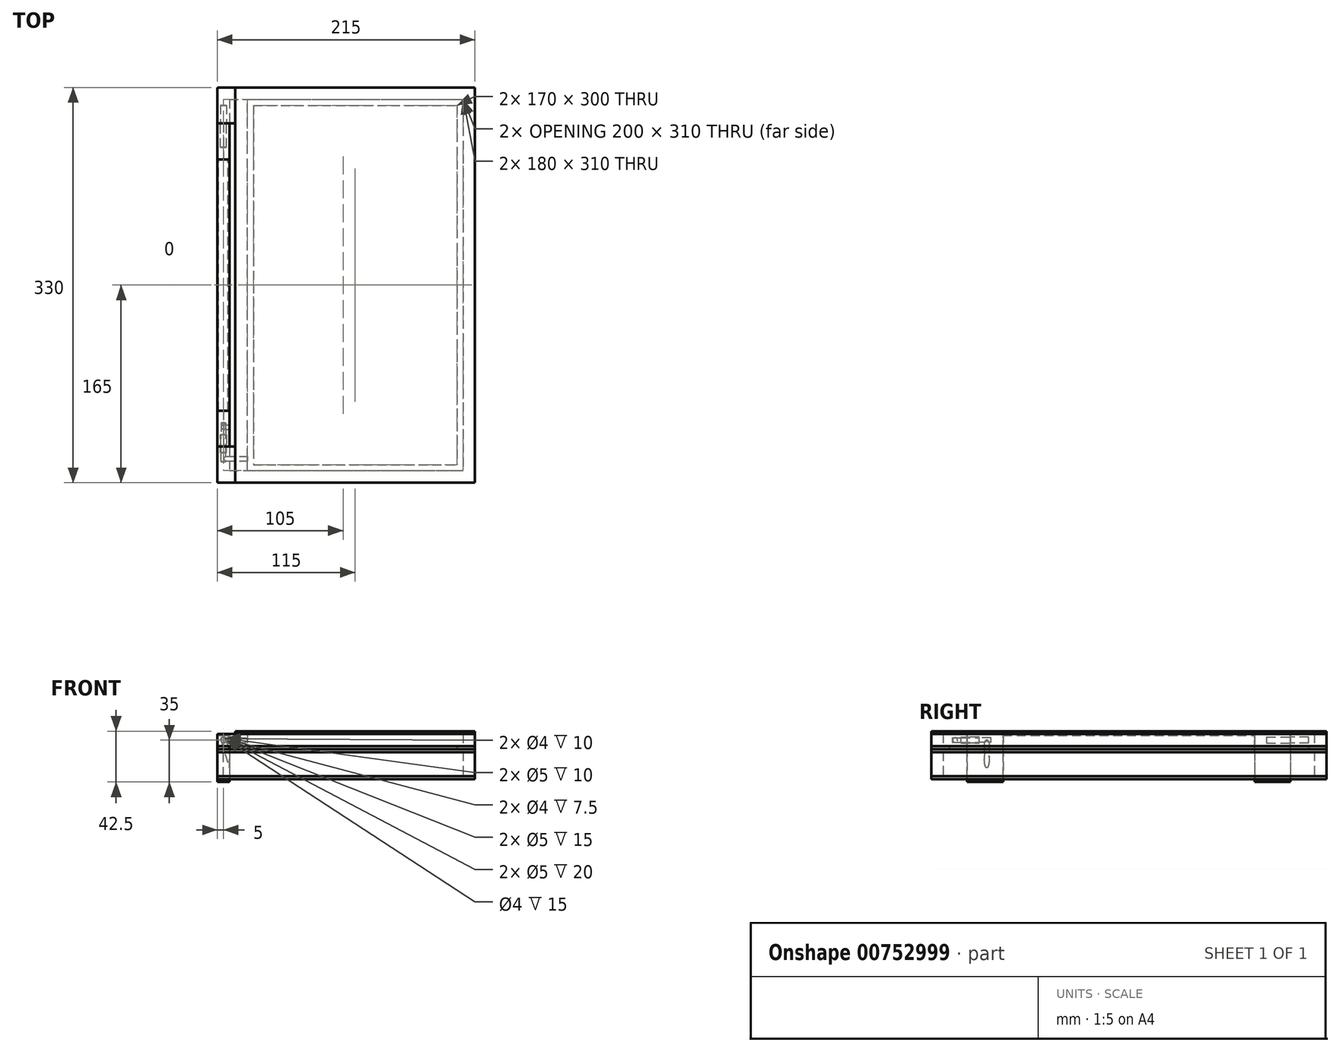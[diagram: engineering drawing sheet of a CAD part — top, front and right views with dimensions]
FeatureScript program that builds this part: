
annotation { "Feature Type Name" : "Feature", "Feature Type Description" : "" }
export const myFeature = defineFeature(function(context is Context, id is Id, definition is map)
    precondition{}
    {
        {
            var Q0;
            Q0=qCreatedBy(makeId("Top.planeOp"),FACE);
            var sketch = newSketch(context, id + "F0", { "sketchPlane" : qUnion([Q0])});
            skLineSegment(sketch, "E0.bottom", {"start": v(0, 0) * mm, "end": v(215, 0) * mm});
            skLineSegment(sketch, "E0.top", {"start": v(0, 330) * mm, "end": v(215, 330) * mm});
            skLineSegment(sketch, "E0.left", {"start": v(0, 0) * mm, "end": v(0, 330) * mm});
            skLineSegment(sketch, "E0.right", {"start": v(215, 0) * mm, "end": v(215, 330) * mm});
            skSolve(sketch);
        }
        {
            var Q0;
            Q0=makeQuery(id+"F0.imprint","IMPRINT",FACE,{"disambiguationData":[TD([[makeQuery(id+"F0.imprint","IMPRINT",EDGE,{"derivedFrom":sQuery(id+"F0.wireOp",EDGE,"E0.bottom")}),1.0]])]});
            extrude(context, id + "F1", {"entities" : qUnion([Q0]), "depth" : 2.5 * mm, "offsetDistance" : 25 * mm});
        }
        {
            var Q0;
            Q0=makeQuery(id+"F1.opExtrude","CAP_FACE",FACE,{"disambiguationData":[OSD([sQuery(id+"F0.wireOp",EDGE,"E0.bottom"),sQuery(id+"F0.wireOp",EDGE,"E0.top"),sQuery(id+"F0.wireOp",EDGE,"E0.left"),sQuery(id+"F0.wireOp",EDGE,"E0.right")])],"isStart":false});
            var sketch = newSketch(context, id + "F2", { "sketchPlane" : qUnion([Q0])});
            skLineSegment(sketch, "E1", {"start": v(215, 0) * mm, "end": v(215, 10) * mm, "construction": true});
            skLineSegment(sketch, "E2", {"start": v(215, 10) * mm, "end": v(205, 10) * mm, "construction": true});
            skLineSegment(sketch, "E3", {"start": v(0, 330) * mm, "end": v(0, 320) * mm, "construction": true});
            skLineSegment(sketch, "E4", {"start": v(0, 320) * mm, "end": v(10, 320) * mm, "construction": true});
            skLineSegment(sketch, "E5.bottom", {"start": v(10, 320) * mm, "end": v(205, 320) * mm});
            skLineSegment(sketch, "E5.top", {"start": v(10, 10) * mm, "end": v(205, 10) * mm});
            skLineSegment(sketch, "E5.left", {"start": v(10, 320) * mm, "end": v(10, 10) * mm});
            skLineSegment(sketch, "E5.right", {"start": v(205, 320) * mm, "end": v(205, 10) * mm});
            skLineSegment(sketch, "E6.bottom", {"start": v(0, 0) * mm, "end": v(215, 0) * mm});
            skLineSegment(sketch, "E6.top", {"start": v(0, 330) * mm, "end": v(215, 330) * mm});
            skLineSegment(sketch, "E6.left", {"start": v(0, 0) * mm, "end": v(0, 330) * mm});
            skLineSegment(sketch, "E6.right", {"start": v(215, 0) * mm, "end": v(215, 330) * mm});
            skSolve(sketch);
        }
        {
            var Q0;
            Q0=qSketchRegion(id+"F2",true);
            extrude(context, id + "F3", {"entities" : qUnion([Q0]), "depth" : 20 * mm, "offsetDistance" : 25 * mm});
        }
        {
            var Q0;
            Q0=qCreatedBy(makeId("Front.planeOp"),FACE);
            var sketch = newSketch(context, id + "F4", { "sketchPlane" : qUnion([Q0])});
            skLineSegment(sketch, "E7", {"start": v(0, 0) * mm, "end": v(0, 2.5) * mm});
            skLineSegment(sketch, "E8", {"start": v(0, 2.5) * mm, "end": v(5, 2.5) * mm});
            skLineSegment(sketch, "E9", {"start": v(5, 2.5) * mm, "end": v(5, 22.5) * mm});
            skLineSegment(sketch, "E10", {"start": v(5, 22.5) * mm, "end": v(0, 22.5) * mm});
            skLineSegment(sketch, "E11", {"start": v(0, 22.5) * mm, "end": v(0, 37.5) * mm});
            skLineSegment(sketch, "E12", {"start": v(0, 37.5) * mm, "end": v(10, 37.5) * mm});
            skLineSegment(sketch, "E13", {"start": v(10, 37.5) * mm, "end": v(10, -2.5) * mm});
            skLineSegment(sketch, "E14", {"start": v(10, -2.5) * mm, "end": v(0, -2.5) * mm});
            skLineSegment(sketch, "E15", {"start": v(0, -2.5) * mm, "end": v(0, 0) * mm});
            skLineSegment(sketch, "E16", {"start": v(5, 37.5) * mm, "end": v(5, 32.5) * mm, "construction": true});
            skCircle(sketch, "E17", {"center": v(5, 32.5) * mm, "radius": 2.5 * mm, "construction": true});
            skSolve(sketch);
        }
        {
            var Q0;
            Q0=qSketchRegion(id+"F4",true);
            extrude(context, id + "F5", {"entities" : qUnion([Q0]), "oppositeDirection" : true, "depth" : 30 * mm, "offsetDistance" : 25 * mm});
        }
        {
            var Q0;
            Q0=makeQuery(id+"F5.opExtrude","SWEPT_BODY",BODY,{"disambiguationData":[OSD([sQuery(id+"F4.wireOp",EDGE,"E7"),sQuery(id+"F4.wireOp",EDGE,"E8"),sQuery(id+"F4.wireOp",EDGE,"E9"),sQuery(id+"F4.wireOp",EDGE,"E10"),sQuery(id+"F4.wireOp",EDGE,"E11"),sQuery(id+"F4.wireOp",EDGE,"E12"),sQuery(id+"F4.wireOp",EDGE,"E13"),sQuery(id+"F4.wireOp",EDGE,"E14"),sQuery(id+"F4.wireOp",EDGE,"E15"),sQuery(id+"F4.wireOp",EDGE,"E17")])]});
            transform(context, id + "F6", {"entities" : qUnion([Q0]), "transformType" : TransformType.TRANSLATION_3D, "dx" : 0 * mm, "dy" : 30 * mm, "dz" : 0 * mm, "makeCopy" : false});
        }
        {
            var Q0;
            Q0=makeQuery(id+"F5.opExtrude","SWEPT_BODY",BODY,{"disambiguationData":[OSD([sQuery(id+"F4.wireOp",EDGE,"E7"),sQuery(id+"F4.wireOp",EDGE,"E8"),sQuery(id+"F4.wireOp",EDGE,"E9"),sQuery(id+"F4.wireOp",EDGE,"E10"),sQuery(id+"F4.wireOp",EDGE,"E11"),sQuery(id+"F4.wireOp",EDGE,"E12"),sQuery(id+"F4.wireOp",EDGE,"E13"),sQuery(id+"F4.wireOp",EDGE,"E14"),sQuery(id+"F4.wireOp",EDGE,"E15"),sQuery(id+"F4.wireOp",EDGE,"E17")])]});
            transform(context, id + "F7", {"entities" : qUnion([Q0]), "transformType" : TransformType.TRANSLATION_3D, "dx" : 0 * mm, "dy" : 240 * mm, "dz" : 0 * mm, "makeCopy" : true});
        }
        {
            var Q0;
            Q0=makeQuery(id+"F3.opExtrude","CAP_FACE",FACE,{"disambiguationData":[OSD([sQuery(id+"F2.wireOp",EDGE,"E5.bottom"),sQuery(id+"F2.wireOp",EDGE,"E5.top"),sQuery(id+"F2.wireOp",EDGE,"E5.left"),sQuery(id+"F2.wireOp",EDGE,"E5.right"),sQuery(id+"F2.wireOp",EDGE,"E6.bottom"),sQuery(id+"F2.wireOp",EDGE,"E6.top"),sQuery(id+"F2.wireOp",EDGE,"E6.left"),sQuery(id+"F2.wireOp",EDGE,"E6.right")])],"isStart":false});
            var sketch = newSketch(context, id + "F8", { "sketchPlane" : qUnion([Q0])});
            skLineSegment(sketch, "E18.bottom", {"start": v(0, 0) * mm, "end": v(215, 0) * mm});
            skLineSegment(sketch, "E18.top", {"start": v(0, 330) * mm, "end": v(215, 330) * mm});
            skLineSegment(sketch, "E18.left", {"start": v(0, 0) * mm, "end": v(0, 330) * mm});
            skLineSegment(sketch, "E18.right", {"start": v(215, 0) * mm, "end": v(215, 330) * mm});
            skSolve(sketch);
        }
        {
            var Q0;
            Q0=qSketchRegion(id+"F8",true);
            extrude(context, id + "F9", {"entities" : qUnion([Q0]), "depth" : 2.5 * mm, "offsetDistance" : 25 * mm});
        }
        {
            var Q0;
            Q0=makeQuery(id+"F7.opPattern","COPY",BODY,{"derivedFrom":makeQuery(id+"F5.opExtrude","SWEPT_BODY",BODY,{"disambiguationData":[OSD([sQuery(id+"F4.wireOp",EDGE,"E7"),sQuery(id+"F4.wireOp",EDGE,"E8"),sQuery(id+"F4.wireOp",EDGE,"E9"),sQuery(id+"F4.wireOp",EDGE,"E10"),sQuery(id+"F4.wireOp",EDGE,"E11"),sQuery(id+"F4.wireOp",EDGE,"E12"),sQuery(id+"F4.wireOp",EDGE,"E13"),sQuery(id+"F4.wireOp",EDGE,"E14"),sQuery(id+"F4.wireOp",EDGE,"E15"),sQuery(id+"F4.wireOp",EDGE,"E17")])]}),"instanceName":"1"});
            var Q1;
            Q1=makeQuery(id+"F5.opExtrude","SWEPT_BODY",BODY,{"disambiguationData":[OSD([sQuery(id+"F4.wireOp",EDGE,"E7"),sQuery(id+"F4.wireOp",EDGE,"E8"),sQuery(id+"F4.wireOp",EDGE,"E9"),sQuery(id+"F4.wireOp",EDGE,"E10"),sQuery(id+"F4.wireOp",EDGE,"E11"),sQuery(id+"F4.wireOp",EDGE,"E12"),sQuery(id+"F4.wireOp",EDGE,"E13"),sQuery(id+"F4.wireOp",EDGE,"E14"),sQuery(id+"F4.wireOp",EDGE,"E15"),sQuery(id+"F4.wireOp",EDGE,"E17")])]});
            var Q2;
            Q2=makeQuery(id+"F3.opExtrude","SWEPT_BODY",BODY,{"disambiguationData":[OSD([sQuery(id+"F2.wireOp",EDGE,"E5.bottom"),sQuery(id+"F2.wireOp",EDGE,"E5.top"),sQuery(id+"F2.wireOp",EDGE,"E5.left"),sQuery(id+"F2.wireOp",EDGE,"E5.right"),sQuery(id+"F2.wireOp",EDGE,"E6.bottom"),sQuery(id+"F2.wireOp",EDGE,"E6.top"),sQuery(id+"F2.wireOp",EDGE,"E6.left"),sQuery(id+"F2.wireOp",EDGE,"E6.right")])]});
            var Q3;
            Q3=makeQuery(id+"F9.opExtrude","SWEPT_BODY",BODY,{"disambiguationData":[OSD([sQuery(id+"F8.wireOp",EDGE,"E18.bottom"),sQuery(id+"F8.wireOp",EDGE,"E18.top"),sQuery(id+"F8.wireOp",EDGE,"E18.left"),sQuery(id+"F8.wireOp",EDGE,"E18.right")])]});
            var Q4;
            Q4=makeQuery(id+"F1.opExtrude","SWEPT_BODY",BODY,{"disambiguationData":[OSD([sQuery(id+"F0.wireOp",EDGE,"E0.bottom"),sQuery(id+"F0.wireOp",EDGE,"E0.top"),sQuery(id+"F0.wireOp",EDGE,"E0.left"),sQuery(id+"F0.wireOp",EDGE,"E0.right")])]});
            booleanBodies(context, id + "F10", {"operationType" : BooleanOperationType.SUBTRACTION, "tools" : qUnion([Q0, Q1]), "targets" : qUnion([Q2, Q3, Q4]), "keepTools" : true});
        }
        {
            var Q0;
            Q0=makeQuery(id+"F9.opExtrude","CAP_FACE",FACE,{"disambiguationData":[OSD([sQuery(id+"F8.wireOp",EDGE,"E18.bottom"),sQuery(id+"F8.wireOp",EDGE,"E18.top"),sQuery(id+"F8.wireOp",EDGE,"E18.left"),sQuery(id+"F8.wireOp",EDGE,"E18.right")])],"isStart":false});
            var sketch = newSketch(context, id + "F11", { "sketchPlane" : qUnion([Q0])});
            skLineSegment(sketch, "E19.bottom", {"start": v(215, 0) * mm, "end": v(15, 0) * mm});
            skLineSegment(sketch, "E19.top", {"start": v(215, 330) * mm, "end": v(15, 330) * mm});
            skLineSegment(sketch, "E19.left", {"start": v(215, 0) * mm, "end": v(215, 330) * mm});
            skLineSegment(sketch, "E19.right", {"start": v(15, 0) * mm, "end": v(15, 330) * mm});
            skLineSegment(sketch, "E20", {"start": v(215, 0) * mm, "end": v(215, 15) * mm, "construction": true});
            skLineSegment(sketch, "E21", {"start": v(215, 15) * mm, "end": v(200, 15) * mm, "construction": true});
            skLineSegment(sketch, "E22", {"start": v(15, 330) * mm, "end": v(15, 315) * mm, "construction": true});
            skLineSegment(sketch, "E23", {"start": v(15, 315) * mm, "end": v(30, 315) * mm, "construction": true});
            skLineSegment(sketch, "E24.bottom", {"start": v(30, 315) * mm, "end": v(200, 315) * mm});
            skLineSegment(sketch, "E24.top", {"start": v(30, 15) * mm, "end": v(200, 15) * mm});
            skLineSegment(sketch, "E24.left", {"start": v(30, 315) * mm, "end": v(30, 15) * mm});
            skLineSegment(sketch, "E24.right", {"start": v(200, 315) * mm, "end": v(200, 15) * mm});
            skSolve(sketch);
        }
        {
            var Q0;
            Q0=qSketchRegion(id+"F11",true);
            extrude(context, id + "F12", {"entities" : qUnion([Q0]), "depth" : 2.5 * mm, "offsetDistance" : 25 * mm});
        }
        {
            var Q0;
            Q0=makeQuery(id+"F12.opExtrude","CAP_FACE",FACE,{"disambiguationData":[OSD([sQuery(id+"F11.wireOp",EDGE,"E19.bottom"),sQuery(id+"F11.wireOp",EDGE,"E19.top"),sQuery(id+"F11.wireOp",EDGE,"E19.left"),sQuery(id+"F11.wireOp",EDGE,"E19.right"),sQuery(id+"F11.wireOp",EDGE,"E24.bottom"),sQuery(id+"F11.wireOp",EDGE,"E24.top"),sQuery(id+"F11.wireOp",EDGE,"E24.left"),sQuery(id+"F11.wireOp",EDGE,"E24.right")])],"isStart":false});
            var sketch = newSketch(context, id + "F13", { "sketchPlane" : qUnion([Q0])});
            skLineSegment(sketch, "E25.bottom", {"start": v(215, 0) * mm, "end": v(0, 0) * mm});
            skLineSegment(sketch, "E25.top", {"start": v(215, 330) * mm, "end": v(0, 330) * mm});
            skLineSegment(sketch, "E25.left", {"start": v(215, 0) * mm, "end": v(215, 330) * mm});
            skLineSegment(sketch, "E25.right", {"start": v(0, 0) * mm, "end": v(0, 330) * mm, "construction": true});
            skLineSegment(sketch, "E26", {"start": v(0, 0) * mm, "end": v(0, 30) * mm});
            skLineSegment(sketch, "E27", {"start": v(0, 30) * mm, "end": v(15, 30) * mm});
            skLineSegment(sketch, "E28", {"start": v(0, 330) * mm, "end": v(0, 300) * mm});
            skLineSegment(sketch, "E29", {"start": v(0, 300) * mm, "end": v(15, 300) * mm});
            skLineSegment(sketch, "E30", {"start": v(15, 300) * mm, "end": v(15, 30) * mm});
            skLineSegment(sketch, "E31", {"start": v(215, 330) * mm, "end": v(215, 320) * mm, "construction": true});
            skLineSegment(sketch, "E32", {"start": v(215, 320) * mm, "end": v(205, 320) * mm, "construction": true});
            skLineSegment(sketch, "E33", {"start": v(15, 30) * mm, "end": v(25, 30) * mm, "construction": true});
            skLineSegment(sketch, "E34", {"start": v(25, 30) * mm, "end": v(25, 10) * mm, "construction": true});
            skLineSegment(sketch, "E35.bottom", {"start": v(25, 10) * mm, "end": v(205, 10) * mm});
            skLineSegment(sketch, "E35.top", {"start": v(25, 320) * mm, "end": v(205, 320) * mm});
            skLineSegment(sketch, "E35.left", {"start": v(25, 10) * mm, "end": v(25, 320) * mm});
            skLineSegment(sketch, "E35.right", {"start": v(205, 10) * mm, "end": v(205, 320) * mm});
            skSolve(sketch);
        }
        {
            var Q0;
            Q0=qSketchRegion(id+"F13",true);
            extrude(context, id + "F14", {"entities" : qUnion([Q0]), "depth" : 10 * mm, "offsetDistance" : 25 * mm});
        }
        {
            var Q0;
            Q0=makeQuery(id+"F14.opExtrude","CAP_FACE",FACE,{"disambiguationData":[OSD([sQuery(id+"F13.wireOp",EDGE,"E25.bottom"),sQuery(id+"F13.wireOp",EDGE,"E25.top"),sQuery(id+"F13.wireOp",EDGE,"E25.left"),sQuery(id+"F13.wireOp",EDGE,"E26"),sQuery(id+"F13.wireOp",EDGE,"E27"),sQuery(id+"F13.wireOp",EDGE,"E28"),sQuery(id+"F13.wireOp",EDGE,"E29"),sQuery(id+"F13.wireOp",EDGE,"E30"),sQuery(id+"F13.wireOp",EDGE,"E35.bottom"),sQuery(id+"F13.wireOp",EDGE,"E35.top"),sQuery(id+"F13.wireOp",EDGE,"E35.left"),sQuery(id+"F13.wireOp",EDGE,"E35.right")])],"isStart":false});
            var sketch = newSketch(context, id + "F15", { "sketchPlane" : qUnion([Q0])});
            skLineSegment(sketch, "E36.bottom", {"start": v(215, 0) * mm, "end": v(15, 0) * mm});
            skLineSegment(sketch, "E36.top", {"start": v(215, 330) * mm, "end": v(15, 330) * mm});
            skLineSegment(sketch, "E36.left", {"start": v(215, 0) * mm, "end": v(215, 330) * mm});
            skLineSegment(sketch, "E36.right", {"start": v(15, 0) * mm, "end": v(15, 330) * mm});
            skSolve(sketch);
        }
        {
            var Q0;
            Q0=qSketchRegion(id+"F15",true);
            extrude(context, id + "F16", {"entities" : qUnion([Q0]), "depth" : 2.5 * mm, "offsetDistance" : 25 * mm});
        }
        {
            var Q0;
            Q0=makeQuery(id+"F7.opPattern","COPY",FACE,{"derivedFrom":makeQuery(id+"F5.opExtrude","CAP_FACE",FACE,{"disambiguationData":[OSD([sQuery(id+"F4.wireOp",EDGE,"E7"),sQuery(id+"F4.wireOp",EDGE,"E8"),sQuery(id+"F4.wireOp",EDGE,"E9"),sQuery(id+"F4.wireOp",EDGE,"E10"),sQuery(id+"F4.wireOp",EDGE,"E11"),sQuery(id+"F4.wireOp",EDGE,"E12"),sQuery(id+"F4.wireOp",EDGE,"E13"),sQuery(id+"F4.wireOp",EDGE,"E14"),sQuery(id+"F4.wireOp",EDGE,"E15"),sQuery(id+"F4.wireOp",EDGE,"E17")])],"isStart":true}),"instanceName":"1"});
            var sketch = newSketch(context, id + "F17", { "sketchPlane" : qUnion([Q0])});
            skLineSegment(sketch, "E37", {"start": v(0, 37.5) * mm, "end": v(0, 25) * mm});
            skLineSegment(sketch, "E38", {"start": v(0, 25) * mm, "end": v(1, 25) * mm});
            skLineSegment(sketch, "E39", {"start": v(1, 25) * mm, "end": v(1, 36.5) * mm});
            skLineSegment(sketch, "E40", {"start": v(1, 36.5) * mm, "end": v(9, 36.5) * mm});
            skLineSegment(sketch, "E41", {"start": v(9, 36.5) * mm, "end": v(9, 25) * mm});
            skLineSegment(sketch, "E42", {"start": v(9, 25) * mm, "end": v(10, 25) * mm});
            skLineSegment(sketch, "E43", {"start": v(10, 25) * mm, "end": v(10, 37.5) * mm});
            skLineSegment(sketch, "E44", {"start": v(10, 37.5) * mm, "end": v(0, 37.5) * mm});
            skSolve(sketch);
        }
        {
            var Q0;
            Q0=qSketchRegion(id+"F17",true);
            extrude(context, id + "F18", {"entities" : qUnion([Q0]), "endBound" : BoundingType.UP_TO_NEXT, "depth" : 25 * mm, "offsetDistance" : 25 * mm});
        }
        {
            var Q0;
            Q0=makeQuery(id+"F14.opExtrude","SWEPT_FACE",FACE,{"disambiguationData":[OSD([sQuery(id+"F13.wireOp",EDGE,"E35.left")])]});
            var sketch = newSketch(context, id + "F19", { "sketchPlane" : qUnion([Q0])});
            skLineSegment(sketch, "E45", {"start": v(10, 32.5) * mm, "end": v(20, 32.5) * mm, "construction": true});
            skCircle(sketch, "E46", {"center": v(20, 32.5) * mm, "radius": 2 * mm});
            skSolve(sketch);
        }
        {
            var Q0;
            Q0=makeQuery(id+"F19.imprint","IMPRINT",FACE,{"disambiguationData":[TD([[makeQuery(id+"F19.imprint","IMPRINT",EDGE,{"derivedFrom":sQuery(id+"F19.wireOp",EDGE,"E46")}),1.0]])]});
            var Q1;
            Q1=sQuery(id+"F19.wireOp",EDGE,"E46");
            extrude(context, id + "F20", {"entities" : qUnion([Q0]), "operationType" : NewBodyOperationType.REMOVE, "surfaceEntities" : qUnion([Q1]), "oppositeDirection" : true, "depth" : 20 * mm, "offsetDistance" : 25 * mm});
        }
        {
            var Q0;
            Q0=makeQuery(id+"F14.opExtrude","SWEPT_FACE",FACE,{"disambiguationData":[OSD([sQuery(id+"F13.wireOp",EDGE,"E27")])]});
            var sketch = newSketch(context, id + "F21", { "sketchPlane" : qUnion([Q0])});
            skLineSegment(sketch, "E47", {"start": v(0, 32.5) * mm, "end": v(-5, 32.5) * mm, "construction": true});
            skCircle(sketch, "E48", {"center": v(-5, 32.5) * mm, "radius": 2.5 * mm});
            skSolve(sketch);
        }
        {
            var Q0;
            Q0 = qSketchRegion(id + "F21", true);
            extrude(context, id + "F22", {"entities" : qUnion([Q0]), "operationType" : NewBodyOperationType.REMOVE, "oppositeDirection" : true, "depth" : 5 * mm, "offsetDistance" : 25 * mm});
        }
        {
            var Q0;
            Q0=makeQuery(id+"F22.boolean.opBoolean","COPY",FACE,{"derivedFrom":makeQuery(id+"F22.opExtrude","CAP_FACE",FACE,{"disambiguationData":[OSD([sQuery(id+"F21.wireOp",EDGE,"E48")])],"isStart":false})});
            var sketch = newSketch(context, id + "F23", { "sketchPlane" : qUnion([Q0])});
            skCircle(sketch, "E49", {"center": v(-5, 32.5) * mm, "radius": 2 * mm});
            skSolve(sketch);
        }
        {
            var Q0;
            Q0 = qSketchRegion(id + "F23", true);
            extrude(context, id + "F24", {"entities" : qUnion([Q0]), "operationType" : NewBodyOperationType.REMOVE, "oppositeDirection" : true, "depth" : 7.5 * mm, "offsetDistance" : 25 * mm});
        }
        {
            var Q0;
            Q0=makeQuery(id+"F5.opExtrude","CAP_FACE",FACE,{"disambiguationData":[OSD([sQuery(id+"F4.wireOp",EDGE,"E7"),sQuery(id+"F4.wireOp",EDGE,"E8"),sQuery(id+"F4.wireOp",EDGE,"E9"),sQuery(id+"F4.wireOp",EDGE,"E10"),sQuery(id+"F4.wireOp",EDGE,"E11"),sQuery(id+"F4.wireOp",EDGE,"E12"),sQuery(id+"F4.wireOp",EDGE,"E13"),sQuery(id+"F4.wireOp",EDGE,"E14"),sQuery(id+"F4.wireOp",EDGE,"E15")])],"isStart":true});
            var sketch = newSketch(context, id + "F25", { "sketchPlane" : qUnion([Q0])});
            skLineSegment(sketch, "E50", {"start": v(5, 37.5) * mm, "end": v(5, 32.5) * mm, "construction": true});
            skCircle(sketch, "E51", {"center": v(5, 32.5) * mm, "radius": 2.5 * mm});
            skSolve(sketch);
        }
        {
            var Q0;
            Q0 = qSketchRegion(id + "F25", true);
            extrude(context, id + "F26", {"entities" : qUnion([Q0]), "operationType" : NewBodyOperationType.REMOVE, "oppositeDirection" : true, "depth" : 10 * mm, "offsetDistance" : 25 * mm});
        }
        {
            var Q0;
            Q0=makeQuery(id+"F26.boolean.opBoolean","COPY",FACE,{"derivedFrom":makeQuery(id+"F26.opExtrude","CAP_FACE",FACE,{"disambiguationData":[OSD([sQuery(id+"F25.wireOp",EDGE,"E51")])],"isStart":false})});
            var sketch = newSketch(context, id + "F27", { "sketchPlane" : qUnion([Q0])});
            skCircle(sketch, "E52", {"center": v(5, 32.5) * mm, "radius": 2 * mm});
            skSolve(sketch);
        }
        {
            var Q0;
            Q0=makeQuery(id+"F27.imprint","IMPRINT",FACE,{"disambiguationData":[TD([[makeQuery(id+"F27.imprint","IMPRINT",EDGE,{"derivedFrom":sQuery(id+"F27.wireOp",EDGE,"E52")}),1.0]])]});
            extrude(context, id + "F28", {"entities" : qUnion([Q0]), "operationType" : NewBodyOperationType.REMOVE, "oppositeDirection" : true, "depth" : 10 * mm, "offsetDistance" : 25 * mm});
        }
        {
            var Q0;
            Q0=makeQuery(id+"F26.boolean.opBoolean","COPY",FACE,{"derivedFrom":makeQuery(id+"F26.opExtrude","CAP_FACE",FACE,{"disambiguationData":[OSD([sQuery(id+"F25.wireOp",EDGE,"E51")])],"isStart":false})});
            extrude(context, id + "F29", {"entities" : qUnion([Q0]), "depth" : 15 * mm, "offsetDistance" : 25 * mm});
        }
        {
            var Q0;
            Q0=qCreatedBy(makeId("Top.planeOp"),FACE);
            var sketch = newSketch(context, id + "F30", { "sketchPlane" : qUnion([Q0])});
            skCircle(sketch, "E53", {"center": v(0, -3.6) * mm, "radius": 2 * mm});
            skSolve(sketch);
        }
        {
            var Q0;
            Q0 = qSketchRegion(id + "F30", true);
            extrude(context, id + "F31", {"entities" : qUnion([Q0]), "depth" : 30 * mm, "offsetDistance" : 25 * mm});
        }
        {
            var Q0;
            Q0=makeQuery(id+"F31.opExtrude","SWEPT_BODY",BODY,{"disambiguationData":[OSD([sQuery(id+"F30.wireOp",EDGE,"E53")])]});
            transform(context, id + "F32", {"entities" : qUnion([Q0]), "transformType" : TransformType.TRANSLATION_3D, "dx" : 10 * mm, "dy" : 50 * mm, "dz" : 0 * mm, "makeCopy" : false});
        }
        {
            var Q0;
            Q0=makeQuery(id+"F31.opExtrude","SWEPT_BODY",BODY,{"disambiguationData":[OSD([sQuery(id+"F30.wireOp",EDGE,"E53")])]});
            var Q1;
            Q1=makeQuery(id+"F5.opExtrude","SWEPT_EDGE",EDGE,{"disambiguationData":[OSD([sQuery(id+"F4.wireOp",EDGE,"E9"),sQuery(id+"F4.wireOp",EDGE,"E10")])]});
            transform(context, id + "F33", {"entities" : qUnion([Q0]), "transformType" : TransformType.ROTATION, "transformAxis" : qUnion([Q1]), "angle" : 17 * degree, "makeCopy" : false});
        }
        {
            var Q0;
            Q0=makeQuery(id+"F31.opExtrude","SWEPT_BODY",BODY,{"disambiguationData":[OSD([sQuery(id+"F30.wireOp",EDGE,"E53")])]});
            transform(context, id + "F34", {"entities" : qUnion([Q0]), "transformType" : TransformType.TRANSLATION_3D, "dx" : -2.6 * mm, "dy" : 0 * mm, "dz" : 1.4 * mm, "makeCopy" : false});
        }
        {
            var Q0;
            Q0=makeQuery(id+"F31.opExtrude","SWEPT_BODY",BODY,{"disambiguationData":[OSD([sQuery(id+"F30.wireOp",EDGE,"E53")])]});
            var Q1;
            Q1=makeQuery(id+"F5.opExtrude","SWEPT_BODY",BODY,{"disambiguationData":[OSD([sQuery(id+"F4.wireOp",EDGE,"E7"),sQuery(id+"F4.wireOp",EDGE,"E8"),sQuery(id+"F4.wireOp",EDGE,"E9"),sQuery(id+"F4.wireOp",EDGE,"E10"),sQuery(id+"F4.wireOp",EDGE,"E11"),sQuery(id+"F4.wireOp",EDGE,"E12"),sQuery(id+"F4.wireOp",EDGE,"E13"),sQuery(id+"F4.wireOp",EDGE,"E14"),sQuery(id+"F4.wireOp",EDGE,"E15")])]});
            booleanBodies(context, id + "F35", {"operationType" : BooleanOperationType.SUBTRACTION, "tools" : qUnion([Q0]), "targets" : qUnion([Q1])});
        }
        {
            var Q0;
            Q0=makeQuery(id+"F7.opPattern","COPY",FACE,{"derivedFrom":makeQuery(id+"F5.opExtrude","CAP_FACE",FACE,{"disambiguationData":[OSD([sQuery(id+"F4.wireOp",EDGE,"E7"),sQuery(id+"F4.wireOp",EDGE,"E8"),sQuery(id+"F4.wireOp",EDGE,"E9"),sQuery(id+"F4.wireOp",EDGE,"E10"),sQuery(id+"F4.wireOp",EDGE,"E11"),sQuery(id+"F4.wireOp",EDGE,"E12"),sQuery(id+"F4.wireOp",EDGE,"E13"),sQuery(id+"F4.wireOp",EDGE,"E14"),sQuery(id+"F4.wireOp",EDGE,"E15")])],"isStart":false}),"instanceName":"1"});
            var sketch = newSketch(context, id + "F36", { "sketchPlane" : qUnion([Q0])});
            skLineSegment(sketch, "E54", {"start": v(-5, 37.5) * mm, "end": v(-5, 32.5) * mm, "construction": true});
            skCircle(sketch, "E55", {"center": v(-5, 32.5) * mm, "radius": 2.5 * mm});
            skSolve(sketch);
        }
        {
            var Q0;
            Q0 = qSketchRegion(id + "F36", true);
            extrude(context, id + "F37", {"entities" : qUnion([Q0]), "operationType" : NewBodyOperationType.REMOVE, "oppositeDirection" : true, "depth" : 20 * mm, "offsetDistance" : 25 * mm});
        }
        {
            var Q0;
            Q0=makeQuery(id+"F14.opExtrude","SWEPT_FACE",FACE,{"disambiguationData":[OSD([sQuery(id+"F13.wireOp",EDGE,"E29")])]});
            var sketch = newSketch(context, id + "F38", { "sketchPlane" : qUnion([Q0])});
            skLineSegment(sketch, "E56", {"start": v(0, 32.5) * mm, "end": v(5, 32.5) * mm, "construction": true});
            skCircle(sketch, "E57", {"center": v(5, 32.5) * mm, "radius": 2.5 * mm});
            skSolve(sketch);
        }
        {
            var Q0;
            Q0 = qSketchRegion(id + "F38", true);
            extrude(context, id + "F39", {"entities" : qUnion([Q0]), "operationType" : NewBodyOperationType.REMOVE, "oppositeDirection" : true, "depth" : 15 * mm, "offsetDistance" : 25 * mm});
        }
    });
